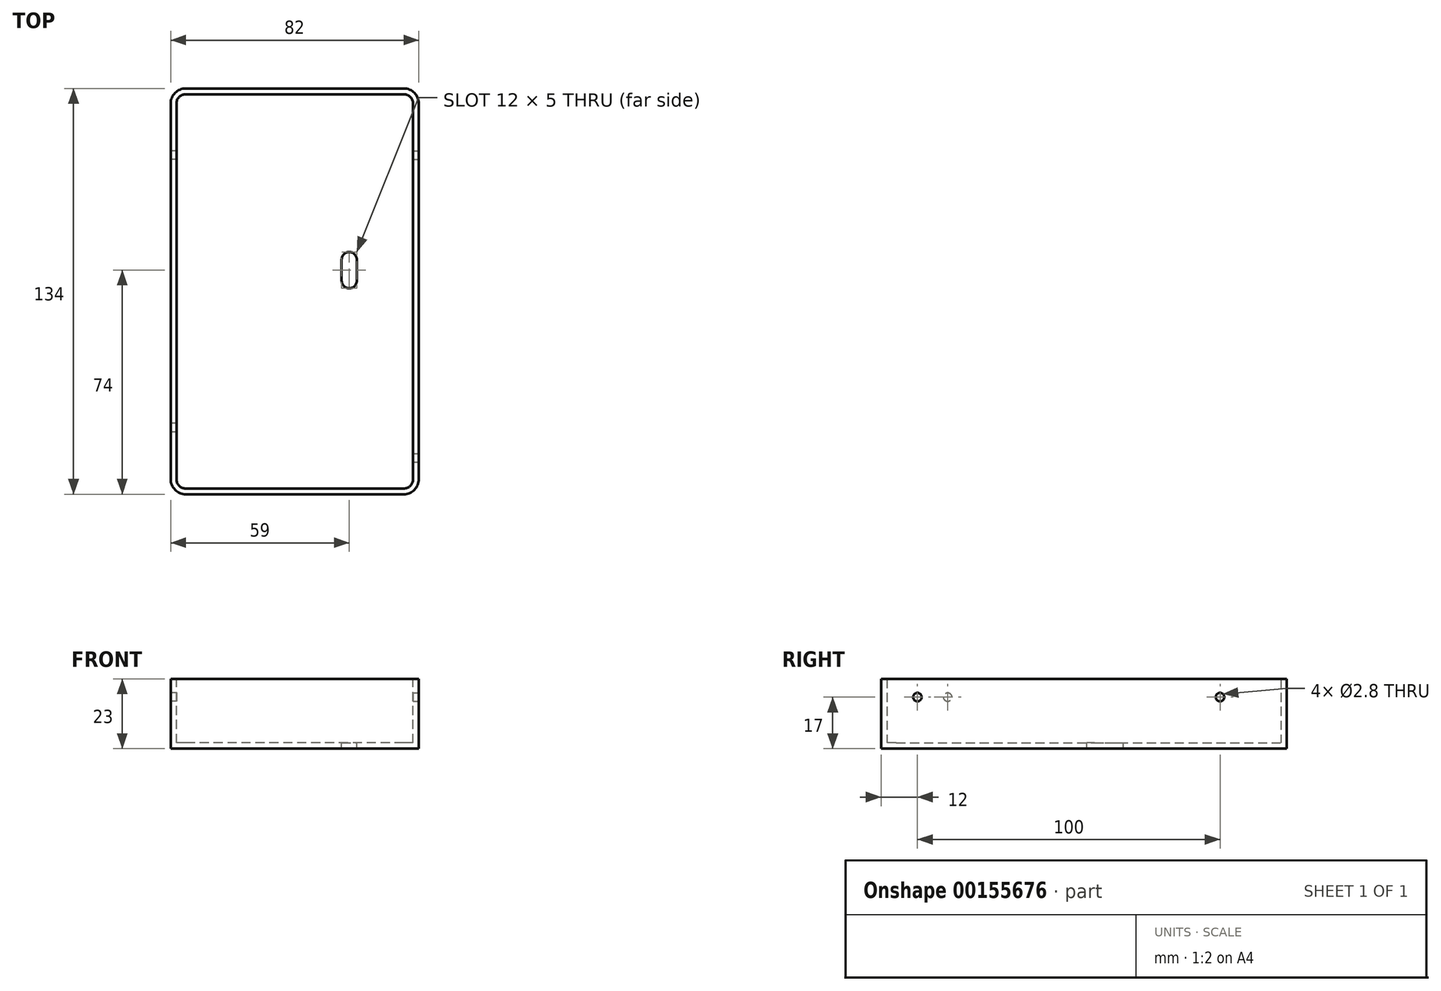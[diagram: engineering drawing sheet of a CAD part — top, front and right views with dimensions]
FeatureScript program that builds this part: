
annotation { "Feature Type Name" : "Feature", "Feature Type Description" : "" }
export const myFeature = defineFeature(function(context is Context, id is Id, definition is map)
    precondition{}
    {
        {
            var Q0;
            Q0=qCreatedBy(makeId("Top.planeOp"),FACE);
            var sketch = newSketch(context, id + "F0", { "sketchPlane" : qUnion([Q0])});
            skLineSegment(sketch, "E0.bottom", {"start": v(36, -67) * mm, "end": v(-36, -67) * mm});
            skLineSegment(sketch, "E0.top", {"start": v(36, 67) * mm, "end": v(-36, 67) * mm});
            skLineSegment(sketch, "E0.left", {"start": v(41, -62) * mm, "end": v(41, 62) * mm});
            skLineSegment(sketch, "E0.right", {"start": v(-41, -62) * mm, "end": v(-41, 62) * mm});
            skPoint(sketch, "E0.middle", {"position": v(0, 0) * mm});
            skPoint(sketch, "E1.visualSharp", {"position": v(-41, 67) * mm});
            skArc(sketch, "E1.filletArc", {"start": v(-36, 67) * mm, "mid": v(-39.54, 65.54) * mm, "end": v(-41, 62) * mm});
            skPoint(sketch, "E2.visualSharp", {"position": v(41, 67) * mm});
            skArc(sketch, "E2.filletArc", {"start": v(41, 62) * mm, "mid": v(39.54, 65.54) * mm, "end": v(36, 67) * mm});
            skPoint(sketch, "E3.visualSharp", {"position": v(41, -67) * mm});
            skArc(sketch, "E3.filletArc", {"start": v(36, -67) * mm, "mid": v(39.54, -65.54) * mm, "end": v(41, -62) * mm});
            skPoint(sketch, "E4.visualSharp", {"position": v(-41, -67) * mm});
            skArc(sketch, "E4.filletArc", {"start": v(-41, -62) * mm, "mid": v(-39.54, -65.54) * mm, "end": v(-36, -67) * mm});
            skSolve(sketch);
        }
        {
            var Q0;
            Q0=qSketchRegion(id+"F0",true);
            extrude(context, id + "F1", {"entities" : qUnion([Q0]), "depth" : 23 * mm});
        }
        {
            var Q0;
            Q0=makeQuery(id+"F1.opExtrude","CAP_FACE",FACE,{"disambiguationData":[OSD([sQuery(id+"F0.wireOp",EDGE,"E0.bottom"),sQuery(id+"F0.wireOp",EDGE,"E0.top"),sQuery(id+"F0.wireOp",EDGE,"E0.left"),sQuery(id+"F0.wireOp",EDGE,"E0.right"),sQuery(id+"F0.wireOp",EDGE,"E1.filletArc"),sQuery(id+"F0.wireOp",EDGE,"E2.filletArc"),sQuery(id+"F0.wireOp",EDGE,"E3.filletArc"),sQuery(id+"F0.wireOp",EDGE,"E4.filletArc")])],"isStart":false});
            shell(context, id + "F2", {"entities" : qUnion([Q0]), "thickness" : 1.9 * mm});
        }
        {
            var Q0;
            Q0=makeQuery(id+"F2.opShell","OFFSET_FACE",FACE,{"disambiguationData":[OSD([sQuery(id+"F0.wireOp",EDGE,"E0.bottom"),sQuery(id+"F0.wireOp",EDGE,"E0.top"),sQuery(id+"F0.wireOp",EDGE,"E0.left"),sQuery(id+"F0.wireOp",EDGE,"E0.right"),sQuery(id+"F0.wireOp",EDGE,"E1.filletArc"),sQuery(id+"F0.wireOp",EDGE,"E2.filletArc"),sQuery(id+"F0.wireOp",EDGE,"E3.filletArc"),sQuery(id+"F0.wireOp",EDGE,"E4.filletArc")])]});
            var sketch = newSketch(context, id + "F3", { "sketchPlane" : qUnion([Q0])});
            skLineSegment(sketch, "E5.left", {"start": v(20.5, 3.5) * mm, "end": v(20.5, 10.5) * mm});
            skLineSegment(sketch, "E5.right", {"start": v(15.5, 3.5) * mm, "end": v(15.5, 10.5) * mm});
            skPoint(sketch, "E5.middle", {"position": v(18, 7) * mm});
            skArc(sketch, "E6", {"start": v(15.5, 10.5) * mm, "mid": v(18, 13) * mm, "end": v(20.5, 10.5) * mm});
            skArc(sketch, "E7", {"start": v(20.5, 3.5) * mm, "mid": v(18, 1) * mm, "end": v(15.5, 3.5) * mm});
            skPoint(sketch, "E8.middle", {"position": v(0, 0) * mm});
            skSolve(sketch);
        }
        {
            var Q0;
            Q0=makeQuery(id+"F3.imprint","IMPRINT",FACE,{"disambiguationData":[TD([[makeQuery(id+"F3.imprint","IMPRINT",EDGE,{"derivedFrom":sQuery(id+"F3.wireOp",EDGE,"E5.left")}),1.0]])]});
            extrude(context, id + "F4", {"entities" : qUnion([Q0]), "operationType" : NewBodyOperationType.REMOVE, "oppositeDirection" : true, "depth" : 2 * mm});
        }
        {
            var Q0;
            Q0=makeQuery(id+"F1.opExtrude","SWEPT_FACE",FACE,{"disambiguationData":[OSD([sQuery(id+"F0.wireOp",EDGE,"E0.right")])]});
            var sketch = newSketch(context, id + "F5", { "sketchPlane" : qUnion([Q0])});
            skCircle(sketch, "E9", {"center": v(-45, 17) * mm, "radius": 1.4 * mm});
            skCircle(sketch, "E10", {"center": v(45, 17) * mm, "radius": 1.4 * mm});
            skSolve(sketch);
        }
        {
            var Q0;
            Q0 = qSketchRegion(id + "F5", true);
            extrude(context, id + "F6", {"entities" : qUnion([Q0]), "operationType" : NewBodyOperationType.REMOVE, "oppositeDirection" : true, "depth" : 2 * mm});
        }
        {
            var Q0;
            Q0=makeQuery(id+"F1.opExtrude","SWEPT_FACE",FACE,{"disambiguationData":[OSD([sQuery(id+"F0.wireOp",EDGE,"E0.left")])]});
            var sketch = newSketch(context, id + "F7", { "sketchPlane" : qUnion([Q0])});
            skCircle(sketch, "E11", {"center": v(-55, 17) * mm, "radius": 1.4 * mm});
            skCircle(sketch, "E12", {"center": v(45, 17) * mm, "radius": 1.4 * mm});
            skSolve(sketch);
        }
        {
            var Q0;
            Q0 = qSketchRegion(id + "F7", true);
            extrude(context, id + "F8", {"entities" : qUnion([Q0]), "operationType" : NewBodyOperationType.REMOVE, "oppositeDirection" : true, "depth" : 2 * mm});
        }
    });
